# Revit family: Water_Heaters_HAJDU_HAJDU-STXL-300CE_1
name_source: partatom
category: Mechanical Equipment
units: mm (PartAtom-declared; Revit-internal decimal feet)

## family parameters
Always vertical = Yes
Classification = None
Cut with Voids When Loaded = No
Maintain Annotation Orientation = No
OmniClass Number = 23.31.29.13
OmniClass Title = Hot Water Tank Heaters
Part Type = Normal
Room Calculation Point = No
Round Connector Dimension = Use Diameter
Shared = No
Work Plane-Based = Yes

## types (1)
- STXL 300CE
    Case Material = Hajdu - Felület - Fehér
    Církulációs csonk = 19.05 mm  [stored 0.0625 ft]
    Default Elevation = 1219.2 mm  [stored 4 ft]
    Description = A nagy teljesítményű, STXL típusú tartályokat kifejezetten hőszivattyús rendszerekhez ajánljuk. Ezek a tárolók alkalmasak bármilyen hőtermelő eszközzel való felfűtésre, de a nagy felületű hőcserélőjüknek köszönhetően különösen célszerűek fűtési-hűtési hőszivattyús rendszerekhez, kondenzációs kazánokhoz és alacsony hőmérsékletű fűtési rendszerekhez. Elektromos fűtőtesttel rendelkezik, mely által használati melegvizet biztosítanak kazán vagy napkollektor nélkül is.
    Elektromos futés teljesítmény = 2000 W
    Elektromos pótfűtés = Beépített
    Energiahatékonysági osztály = C
    Felfutési ido elektromos futovel = 9 h
    Feszültség = 230 V
    Frekvencia = 50 Hz
    Fázisok száma = 1
    Hocserélo csatlakozás = 25.4 mm  [stored 0.0833333 ft]
    Hocserélo felulete = 3,3 m2
    Hocserélo névleges urtartalma = 23.1 l
    Hocserélo tartós teljesítmény = 99 kW
    Homéro csonk = 12.7 mm  [stored 0.0416667 ft]
    Látszólagos terhelés = 2070 VA
    Magasság = 1530 mm  [stored 5.01969 ft]
    Manufacturer = HAJDU
    Max. vízhomérséklet = 65 °C
    Model = HAJDU STXL 300CE
    Névleges urtartalom = 300 l
    Product Page URL = https://hajdurt.hu
    Rádiusz = 330 mm  [stored 1.08268 ft]
    Teljesítménytényezo = 1
    Tárolási veszteség = 94 W
    Tömeg = 161.00 kg
    URL = https://hajdurt.hu
    Vízcsatlakozás = 19.05 mm  [stored 0.0625 ft]
    Áramfelvétel = 9 A
    Átméro = 660 mm
    Érintésvédelmi osztály = I.
    Érzékelo tokcso = 12 mm  [stored 0.0393701 ft]
    Üzemi nyomás = 1.0 MPa

note: [stored X ft] marks values corroborated as IEEE doubles in the binary element streams (Revit-internal decimal feet)

## geometry (parser evidence)
native form markers: Sweep x3
no freeform markers — native parametric forms only
